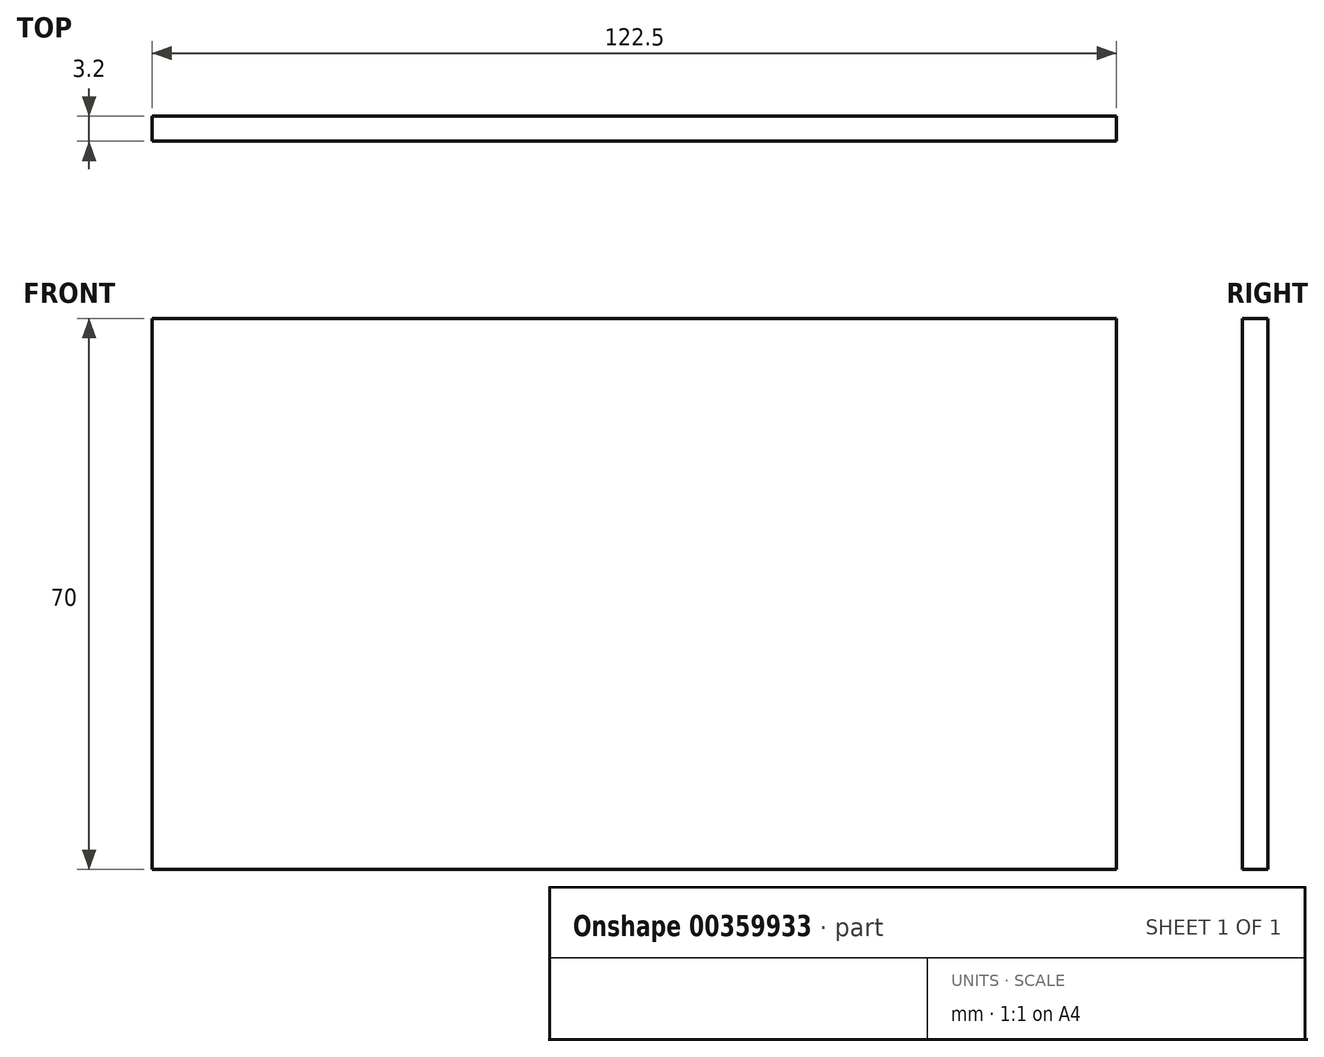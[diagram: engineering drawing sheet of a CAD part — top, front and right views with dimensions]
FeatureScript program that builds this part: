
annotation { "Feature Type Name" : "Feature", "Feature Type Description" : "" }
export const myFeature = defineFeature(function(context is Context, id is Id, definition is map)
    precondition{}
    {
        {
            var Q0;
            Q0=qCreatedBy(makeId("Top.planeOp"),FACE);
            var sketch = newSketch(context, id + "F0", { "sketchPlane" : qUnion([Q0])});
            skLineSegment(sketch, "E0.bottom", {"start": v(-14.69, 2.6) * mm, "end": v(107.81, 2.6) * mm});
            skLineSegment(sketch, "E0.top", {"start": v(-14.69, -0.6) * mm, "end": v(107.81, -0.6) * mm});
            skLineSegment(sketch, "E0.left", {"start": v(-14.69, 2.6) * mm, "end": v(-14.69, -0.6) * mm});
            skLineSegment(sketch, "E0.right", {"start": v(107.81, 2.6) * mm, "end": v(107.81, -0.6) * mm});
            skSolve(sketch);
        }
        {
            var Q0;
            Q0=makeQuery(id+"F0.imprint","IMPRINT",FACE,{"disambiguationData":[TD([[makeQuery(id+"F0.imprint","IMPRINT",EDGE,{"derivedFrom":sQuery(id+"F0.wireOp",EDGE,"E0.bottom")}),-1.0]])]});
            extrude(context, id + "F1", {"entities" : qUnion([Q0]), "depth" : 70 * mm});
        }
    });
